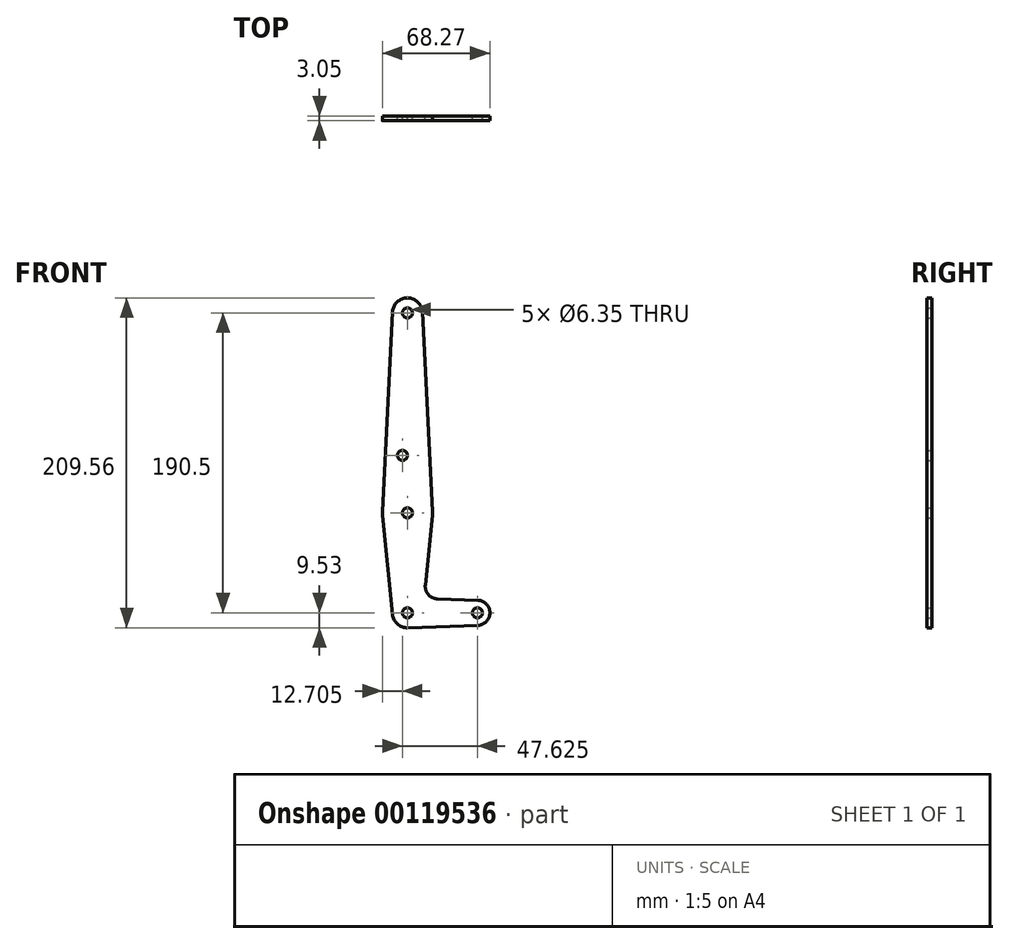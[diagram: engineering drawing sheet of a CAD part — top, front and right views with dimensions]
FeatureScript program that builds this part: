
annotation { "Feature Type Name" : "Feature", "Feature Type Description" : "" }
export const myFeature = defineFeature(function(context is Context, id is Id, definition is map)
    precondition{}
    {
        {
            var Q0;
            Q0=qCreatedBy(makeId("Front.planeOp"),FACE);
            var sketch = newSketch(context, id + "F0", { "sketchPlane" : qUnion([Q0])});
            skCircle(sketch, "E0", {"center": v(0, 0) * mm, "radius": 15.88 * mm});
            skCircle(sketch, "E1", {"center": v(0, 127) * mm, "radius": 9.53 * mm});
            skCircle(sketch, "E2", {"center": v(0, -63.5) * mm, "radius": 9.53 * mm});
            skCircle(sketch, "E3", {"center": v(44.45, -63.5) * mm, "radius": 7.94 * mm});
            skArc(sketch, "E4", {"start": v(11.34, -45.9) * mm, "mid": v(13.26, -51.93) * mm, "end": v(18.97, -54.65) * mm});
            skLineSegment(sketch, "E5", {"start": v(9.51, 127.48) * mm, "end": v(15.86, 0.8) * mm});
            skLineSegment(sketch, "E6", {"start": v(-9.51, 127.48) * mm, "end": v(-15.86, 0.8) * mm});
            skLineSegment(sketch, "E7", {"start": v(-15.8, -1.59) * mm, "end": v(-9.48, -64.45) * mm});
            skLineSegment(sketch, "E8", {"start": v(15.8, -1.59) * mm, "end": v(11.34, -45.9) * mm});
            skLineSegment(sketch, "E9", {"start": v(18.97, -54.65) * mm, "end": v(44.73, -55.57) * mm});
            skLineSegment(sketch, "E10", {"start": v(0.34, -73.02) * mm, "end": v(44.73, -71.43) * mm});
            skCircle(sketch, "E11", {"center": v(-3.18, 36.53) * mm, "radius": 3.18 * mm});
            skCircle(sketch, "E12", {"center": v(0, 127) * mm, "radius": 3.18 * mm});
            skCircle(sketch, "E13", {"center": v(0, 0) * mm, "radius": 3.18 * mm});
            skCircle(sketch, "E14", {"center": v(0, -63.5) * mm, "radius": 3.18 * mm});
            skCircle(sketch, "E15", {"center": v(44.45, -63.5) * mm, "radius": 3.18 * mm});
            skSolve(sketch);
        }
        {
            var Q0;
            Q0=makeQuery(id+"F0.imprint","IMPRINT",FACE,{"disambiguationData":[TD([[makeQuery(id+"F0.imprint","IMPRINT",EDGE,{"derivedFrom":sQuery(id+"F0.wireOp",EDGE,"E14")}),-1.0]])]});
            var Q1;
            Q1=makeQuery(id+"F0.imprint","IMPRINT",FACE,{"disambiguationData":[TD([[makeQuery(id+"F0.imprint","IMPRINT",EDGE,{"derivedFrom":sQuery(id+"F0.wireOp",EDGE,"E15")}),-1.0]])]});
            var Q2;
            Q2=makeQuery(id+"F0.imprint","IMPRINT",FACE,{"disambiguationData":[TD([[makeQuery(id+"F0.imprint","IMPRINT",EDGE,{"derivedFrom":sQuery(id+"F0.wireOp",EDGE,"E13")}),-1.0]])]});
            var Q3;
            Q3=makeQuery(id+"F0.imprint","IMPRINT",FACE,{"disambiguationData":[TD([[makeQuery(id+"F0.imprint","IMPRINT",EDGE,{"derivedFrom":sQuery(id+"F0.wireOp",EDGE,"E4")}),-1.0]])]});
            var Q4;
            {var subQ1=sQuery(id+"F0.wireOp",EDGE,"E5");Q4=makeQuery(id+"F0.imprint","IMPRINT",FACE,{"disambiguationData":[TD([[makeQuery(id+"F0.imprint","IMPRINT",EDGE,{"derivedFrom":subQ1}),-1.0]])]});}
            var Q5;
            Q5=makeQuery(id+"F0.imprint","IMPRINT",FACE,{"disambiguationData":[TD([[makeQuery(id+"F0.imprint","IMPRINT",EDGE,{"derivedFrom":sQuery(id+"F0.wireOp",EDGE,"E12")}),-1.0]])]});
            extrude(context, id + "F1", {"entities" : qUnion([Q0, Q1, Q2, Q3, Q4, Q5]), "depth" : 3.05 * mm});
        }
    });
